# Revit family: Water_Heaters_HAJDU_HAJDU-STXL-120C-160C_
name_source: partatom
category: Mechanical Equipment
units: mm (PartAtom-declared; Revit-internal decimal feet)

## family parameters
Always vertical = Yes
Classification = None
Cut with Voids When Loaded = No
Maintain Annotation Orientation = No
OmniClass Number = 23.31.29.13
OmniClass Title = Hot Water Tank Heaters
Part Type = Normal
Room Calculation Point = No
Round Connector Dimension = Use Diameter
Shared = No
Work Plane-Based = Yes

## types (2) — shared parameters
Case Material = Hajdu - Felület - Fehér
Církulációs csonk = 19.05 mm  [stored 0.0625 ft]
Default Elevation = 1219.2 mm  [stored 4 ft]
Description = A nagy teljesítményű, STXL típusú tartályokat kifejezetten hőszivattyús rendszerekhez ajánljuk. Ezek a tárolók alkalmasak bármilyen hőtermelő eszközzel való felfűtésre, de a nagy felületű hőcserélőjüknek köszönhetően különösen célszerűek fűtési-hűtési hőszivattyús rendszerekhez, kondenzációs kazánokhoz és alacsony hőmérsékletű fűtési rendszerekhez. A készülékbe elektromos pótfűtés szerelhető be utólagosan. ( A pótfűtés szett külön megvásárolható)
Energiahatékonysági osztály = B
Hocserélo csatlakozás = 31.75 mm
Homéro csonk = 12.7 mm  [stored 0.0416667 ft]
Korrózióvédelem = tűzzománc + aktív anód
Manufacturer = HAJDU
Product Page URL = https://hajdurt.hu
Rádiusz = 297.5 mm  [stored 0.97605 ft]
Tartály = tűzzománcozott acéllemez
URL = https://hajdurt.hu
Vízcsatlakozás = 25.4 mm  [stored 0.0833333 ft]
Átméro = 595 mm  [stored 1.9521 ft]
Érzékelo tokcso = 12 mm  [stored 0.0393701 ft]
Üzemi nyomás = 1.0 MPa

## per-type parameters (varying)
| type | Csatlakozó magassága "A" | Csatlakozó magassága "B" | Csatlakozó magassága "C" | Csatlakozó magassága "D" | Hocserélo felulete | Hocserélo névleges urtartalma | Hocserélo tartós teljesítmény | Magasság | Névleges urtartalom | Tárolási veszteség | Tömeg |
| STXL 120C | 415 mm  [stored 1.36155 ft] | 661 mm  [stored 2.16864 ft] | 770 mm  [stored 2.52625 ft] | 870 mm  [stored 2.85433 ft] | 1.44 m2 | 10 l | 43 kW | 1150 mm | 120 l | 50 W | 88.00 kg |
| STXL 160C | 495 mm  [stored 1.62402 ft] | 821 mm  [stored 2.69357 ft] | 1010 mm  [stored 3.31365 ft] | 1110 mm  [stored 3.64173 ft] | 2.05 m2 | 14.3 l | 62 kW | 1390 mm  [stored 4.56037 ft] | 160 l | 57 W | 107.00 kg |

note: column(s) folded — value = type name in every type: Model

note: [stored X ft] marks values corroborated as IEEE doubles in the binary element streams (Revit-internal decimal feet)

## geometry (parser evidence)
native form markers: Sweep x4
no freeform markers — native parametric forms only
